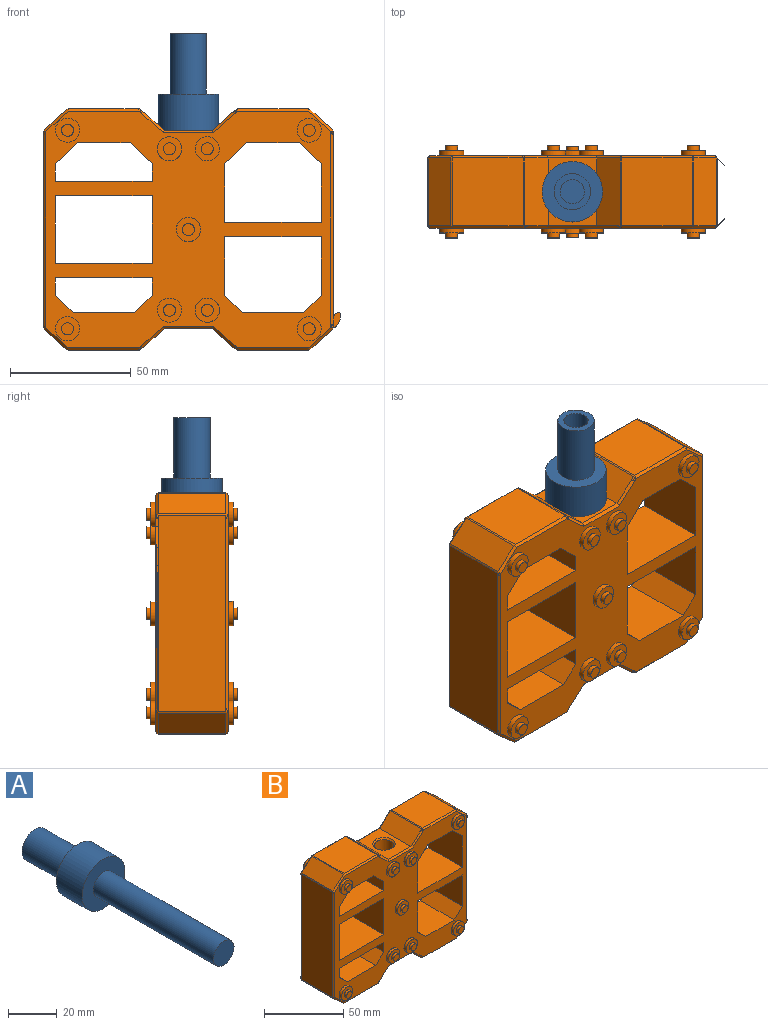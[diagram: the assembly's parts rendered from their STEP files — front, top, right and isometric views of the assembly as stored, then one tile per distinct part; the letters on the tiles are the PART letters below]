
ASSEMBLY  parts=2 mates=1
PART A: 9 faces, bbox 25x110x25 mm
  f0: cylinder r=6mm len=70mm, axis (0,1,0), area 2638.9mm2, adj f1,f4
  f1: plane 12x12mm, normal (0,-1,0), area 113.1mm2, adj f0
  f2: cylinder r=12.5mm len=25mm, axis (0,-1,0), area 1178.1mm2, adj f3,f4
  f3: plane 25x25mm, normal (0,1,0), area 314.2mm2, adj f2,f5
  f4: plane 25x25mm, normal (0,-1,0), area 377.8mm2, adj f0,f2
  f5: cylinder r=7.5mm len=25mm, axis (0,-1,0), area 1178.1mm2, adj f3,f6
  f6: plane 15x15mm, normal (0,1,0), area 98.2mm2, adj f5,f7
  f7: cylinder r=5mm len=25mm, axis (0,1,0), area 785.4mm2, adj f6,f8
  f8: plane 10x10mm, normal (0,1,0), area 78.5mm2, adj f7
PART B: 248 faces, bbox 132.8x46x108 mm
  f0: plane 26.18x0.53mm, normal (-0.18,0,-0.98), area 9mm2, adj f1,f245,f246,f247
  f1: cylinder r=2mm len=0.89mm, axis (-1,0,0), area 0.1mm2, adj f0,f2,f3
  f2: bspline ~2.39x1.21mm, area 0.1mm2, adj f1,f3,f247
  f3: plane 1.1x0.46mm, normal (-0.18,0,-0.98), area 0.3mm2, adj f1,f2,f4,f245,f247
  f4: plane 1x1mm, normal (-0.13,-0.7,-0.7), area 0.3mm2, adj f3,f5,f244
  f5: plane 1.06x1mm, normal (-0.25,-0.71,-0.66), area 0.6mm2, adj f4,f6,f7,f241,f243,f247
  f6: plane 1.28x0.99mm, normal (-0.47,-0.71,-0.53), area 0.2mm2, adj f5,f7,f243
  f7: plane 118x98mm, normal (0,-1,0), area 5531mm2, adj f5,f6,f8,f144,f145,f146,f147,f148
  f8: plane 30x24.21mm, normal (1,0,0), area 726.4mm2, adj f7,f9,f144,f148
  f9: plane 118x98mm, normal (0,1,0), area 5531mm2, adj f8,f10,f14,f18,f22,f26,f30,f34
  f10: cylinder r=5mm len=10mm, axis (0,-1,0), area 62.8mm2, adj f9,f11
  f11: plane 10x10mm, normal (0,1,0), area 58.9mm2, adj f10,f12
  f12: cylinder r=2.5mm len=5mm, axis (0,-1,0), area 31.4mm2, adj f11,f13
  f13: plane 5x5mm, normal (0,1,0), area 19.6mm2, adj f12
  f14: cylinder r=5mm len=10mm, axis (0,-1,0), area 62.8mm2, adj f9,f15
  f15: plane 10x10mm, normal (0,1,0), area 58.9mm2, adj f14,f16
  f16: cylinder r=2.5mm len=5mm, axis (0,-1,0), area 31.4mm2, adj f15,f17
  f17: plane 5x5mm, normal (0,1,0), area 19.6mm2, adj f16
  f18: cylinder r=5mm len=10mm, axis (0,-1,0), area 62.8mm2, adj f9,f19
  f19: plane 10x10mm, normal (0,1,0), area 58.9mm2, adj f18,f20
  f20: cylinder r=2.5mm len=5mm, axis (0,-1,0), area 31.4mm2, adj f19,f21
  f21: plane 5x5mm, normal (0,1,0), area 19.6mm2, adj f20
  f22: cylinder r=5mm len=10mm, axis (0,-1,0), area 62.8mm2, adj f9,f23
  f23: plane 10x10mm, normal (0,1,0), area 58.9mm2, adj f22,f24
  f24: cylinder r=2.5mm len=5mm, axis (0,-1,0), area 31.4mm2, adj f23,f25
  f25: plane 5x5mm, normal (0,1,0), area 19.6mm2, adj f24
  f26: cylinder r=5mm len=10mm, axis (0,-1,0), area 62.8mm2, adj f9,f27
  f27: plane 10x10mm, normal (0,1,0), area 58.9mm2, adj f26,f28
  f28: cylinder r=2.5mm len=5mm, axis (0,-1,0), area 31.4mm2, adj f27,f29
  f29: plane 5x5mm, normal (0,1,0), area 19.6mm2, adj f28
  f30: cylinder r=5mm len=10mm, axis (0,-1,0), area 62.8mm2, adj f9,f31
  f31: plane 10x10mm, normal (0,1,0), area 58.9mm2, adj f30,f32
  f32: cylinder r=2.5mm len=5mm, axis (0,-1,0), area 31.4mm2, adj f31,f33
  f33: plane 5x5mm, normal (0,1,0), area 19.6mm2, adj f32
  f34: cylinder r=5mm len=10mm, axis (0,-1,0), area 62.8mm2, adj f9,f35
  f35: plane 10x10mm, normal (0,1,0), area 58.9mm2, adj f34,f36
  f36: cylinder r=2.5mm len=5mm, axis (0,-1,0), area 31.4mm2, adj f35,f37
  f37: plane 5x5mm, normal (0,1,0), area 19.6mm2, adj f36
  f38: cylinder r=5mm len=10mm, axis (0,-1,0), area 62.8mm2, adj f9,f39
  f39: plane 10x10mm, normal (0,1,0), area 58.9mm2, adj f38,f40
  f40: cylinder r=2.5mm len=5mm, axis (0,-1,0), area 31.4mm2, adj f39,f41
  f41: plane 5x5mm, normal (0,1,0), area 19.6mm2, adj f40
  f42: cylinder r=5mm len=10mm, axis (0,-1,0), area 62.8mm2, adj f9,f43
  f43: plane 10x10mm, normal (0,1,0), area 58.9mm2, adj f42,f44
  f44: cylinder r=2.5mm len=5mm, axis (0,-1,0), area 31.4mm2, adj f43,f45
  f45: plane 5x5mm, normal (0,1,0), area 19.6mm2, adj f44
  f46: plane 10.05x9.1mm, normal (0.47,0.71,0.53), area 17.8mm2, adj f9,f47,f58,f100
  f47: plane 1x1mm, normal (0.67,0.67,0.3), area 0.6mm2, adj f46,f48,f138
  f48: plane 28x0.75mm, normal (0.91,0,0.41), area 22.9mm2, adj f47,f49,f50,f58
  f49: plane 1x1mm, normal (0.67,-0.67,0.3), area 0.6mm2, adj f48,f207,f236
  f50: plane 81.28x28mm, normal (1,0,0), area 2276mm2, adj f48,f51,f138,f236
  f51: plane 28x0.75mm, normal (0.91,0,-0.41), area 22.9mm2, adj f50,f52,f53,f54
  f52: plane 1x1mm, normal (0.67,-0.67,-0.3), area 0.6mm2, adj f51,f235,f236
  f53: plane 1x1mm, normal (0.67,0.67,-0.3), area 0.6mm2, adj f51,f137,f138
  f54: plane 28x9.38mm, normal (0.67,0,-0.75), area 351.8mm2, adj f51,f55,f137,f235
  f55: plane 28x0.67mm, normal (0.36,0,-0.93), area 19.9mm2, adj f54,f56,f57,f245
  f56: plane 1x1mm, normal (0.26,-0.68,-0.68), area 0.5mm2, adj f55,f235,f244
  f57: plane 1x1mm, normal (0.26,0.68,-0.68), area 0.5mm2, adj f55,f136,f137
  f58: plane 28x9.38mm, normal (0.67,0,0.75), area 351.8mm2, adj f46,f48,f59,f207
  f59: plane 28x0.67mm, normal (0.36,0,0.93), area 19.9mm2, adj f58,f60,f61,f100
  f60: plane 1x1mm, normal (0.26,-0.68,0.68), area 0.5mm2, adj f59,f207,f208
  f61: plane 29.24x28mm, normal (0,0,1), area 818.7mm2, adj f59,f62,f101,f208
  f62: plane 28x0.67mm, normal (-0.36,0,0.93), area 19.9mm2, adj f61,f63,f102,f209
  f63: plane 28x9.72mm, normal (-0.67,0,0.75), area 364.3mm2, adj f62,f64,f106,f213
  f64: plane 28x20mm, normal (0,0,1), area 406.1mm2, adj f63,f65,f99,f107,f214
  f65: plane 28x9.72mm, normal (0.67,0,0.75), area 364.3mm2, adj f64,f66,f108,f215
  f66: plane 28x0.67mm, normal (0.36,0,0.93), area 19.9mm2, adj f65,f67,f112,f219
  f67: plane 29.24x28mm, normal (0,0,1), area 818.7mm2, adj f66,f68,f113,f220
  f68: plane 28x0.67mm, normal (-0.36,0,0.93), area 19.9mm2, adj f67,f69,f70,f98
  f69: plane 1x1mm, normal (-0.26,-0.68,0.68), area 0.5mm2, adj f68,f220,f221
  f70: plane 28x9.38mm, normal (-0.67,0,0.75), area 351.8mm2, adj f68,f71,f114,f221
  f71: plane 28x0.75mm, normal (-0.91,0,0.41), area 22.9mm2, adj f70,f72,f73,f97
  f72: plane 1x1mm, normal (-0.67,-0.67,0.3), area 0.6mm2, adj f71,f221,f222
  f73: plane 81.28x28mm, normal (-1,0,0), area 2276mm2, adj f71,f74,f115,f222
  f74: plane 28x0.75mm, normal (-0.91,0,-0.41), area 22.9mm2, adj f73,f75,f76,f96
  f75: plane 1x1mm, normal (-0.67,-0.67,-0.3), area 0.6mm2, adj f74,f222,f227
  f76: plane 28x9.38mm, normal (-0.67,0,-0.75), area 351.8mm2, adj f74,f77,f120,f227
  f77: plane 28x0.67mm, normal (-0.36,0,-0.93), area 19.9mm2, adj f76,f78,f79,f95
  f78: plane 1x1mm, normal (-0.26,-0.68,-0.68), area 0.5mm2, adj f77,f227,f228
  f79: plane 29.05x28mm, normal (0,0,-1), area 813.5mm2, adj f77,f80,f92,f94,f121,f228
  f80: plane 1.1x0.46mm, normal (0.18,0,-0.98), area 0.3mm2, adj f79,f81,f89,f90,f91
  f81: plane 28x0.5mm, normal (0.36,0,-0.93), area 14.8mm2, adj f80,f82,f87,f91,f92,f94,f122,f229
  f82: plane 28x9.72mm, normal (0.67,0,-0.75), area 364.3mm2, adj f81,f83,f126,f233
  f83: plane 28x20mm, normal (0,0,-1), area 406.1mm2, adj f82,f84,f85,f127,f234
  f84: plane 28x9.72mm, normal (-0.67,0,-0.75), area 364.3mm2, adj f83,f128,f241,f247
  f85: cone r=7mm half-angle=45deg, axis (0,0,-1), area 57.8mm2, adj f83,f86
  f86: cylinder r=6mm len=80.18mm, axis (0,0,1), area 3022.8mm2, adj f85,f99
  f87: bspline ~2.39x1.21mm, area 0.1mm2, adj f81,f88,f92,f94
  f88: cylinder r=2mm len=0.89mm, axis (-1,0,0), area 0.1mm2, adj f87,f92,f94
  f89: plane 1x1mm, normal (0.13,0.7,-0.7), area 0.3mm2, adj f80,f121,f122
  f90: cylinder r=2mm len=0.89mm, axis (-1,0,0), area 0.1mm2, adj f80,f91,f94
  f91: bspline ~2.39x1.21mm, area 0.1mm2, adj f80,f81,f90
  f92: plane 1.1x0.46mm, normal (0.18,0,-0.98), area 0.3mm2, adj f79,f81,f87,f88,f93
  f93: plane 1x1mm, normal (0.13,-0.7,-0.7), area 0.3mm2, adj f92,f228,f229
  f94: plane 26.17x0.53mm, normal (0.18,0,-0.98), area 9mm2, adj f79,f81,f87,f88,f90
  f95: plane 1x1mm, normal (-0.26,0.68,-0.68), area 0.5mm2, adj f77,f120,f121
  f96: plane 1x1mm, normal (-0.67,0.67,-0.3), area 0.6mm2, adj f74,f115,f120
  f97: plane 1x1mm, normal (-0.67,0.67,0.3), area 0.6mm2, adj f71,f114,f115
  f98: plane 1x1mm, normal (-0.26,0.68,0.68), area 0.5mm2, adj f68,f113,f114
  f99: cone r=6mm half-angle=45deg, axis (0,0,1), area 57.8mm2, adj f64,f86
  f100: plane 1x1mm, normal (0.26,0.68,0.68), area 0.5mm2, adj f46,f59,f101
  f101: plane 29.24x1mm, normal (0,0.71,0.71), area 41.2mm2, adj f9,f61,f100,f102
  f102: plane 1.13x1mm, normal (-0.25,0.71,0.66), area 0.7mm2, adj f9,f62,f101,f103,f104,f105,f106
  f103: bspline ~1.4x1.27mm, area 1mm2, adj f102,f104,f106
  f104: cylinder r=2mm len=1.34mm, axis (1,0,0), area 0.2mm2, adj f102,f103,f105
  f105: plane 1.28x0.99mm, normal (-0.47,0.71,0.53), area 0.2mm2, adj f9,f102,f104
  f106: plane 10.02x9.69mm, normal (-0.47,0.71,0.53), area 17.2mm2, adj f9,f63,f102,f103,f107
  f107: plane 20.76x1mm, normal (0,0.71,0.71), area 28.8mm2, adj f9,f64,f106,f108
  f108: plane 10.02x9.69mm, normal (0.47,0.71,0.53), area 17.2mm2, adj f9,f65,f107,f109,f112
  f109: bspline ~1.4x1.27mm, area 1mm2, adj f108,f110,f112
  f110: cylinder r=2mm len=1.34mm, axis (1,0,0), area 0.2mm2, adj f109,f111,f112
  f111: plane 1.28x0.99mm, normal (0.47,0.71,0.53), area 0.2mm2, adj f9,f110,f112
  f112: plane 1.13x1mm, normal (0.25,0.71,0.66), area 0.7mm2, adj f9,f66,f108,f109,f110,f111,f113
  f113: plane 29.24x1mm, normal (0,0.71,0.71), area 41.2mm2, adj f9,f67,f98,f112
  f114: plane 10.05x9.1mm, normal (-0.47,0.71,0.53), area 17.8mm2, adj f9,f70,f97,f98
  f115: plane 81.59x1.31mm, normal (-0.71,0.71,0), area 113mm2, adj f9,f73,f96,f97,f116,f117,f118,f119
  f116: bspline ~1.86x1.48mm, area 0.8mm2, adj f115,f117
  f117: cylinder r=2mm len=1.25mm, axis (0.75,0,0.67), area 0mm2, adj f115,f116
  f118: cylinder r=2mm len=1.25mm, axis (-0.75,0,0.67), area 0mm2, adj f115,f119
  f119: bspline ~1.86x1.48mm, area 0.8mm2, adj f115,f118
  f120: plane 10.05x9.1mm, normal (-0.47,0.71,-0.53), area 17.8mm2, adj f9,f76,f95,f96
  f121: plane 29.05x1mm, normal (0,0.71,-0.71), area 41.1mm2, adj f9,f79,f89,f95
  f122: plane 1.06x1mm, normal (0.25,0.71,-0.66), area 0.6mm2, adj f9,f81,f89,f123,f125,f126
  f123: cylinder r=2mm len=1.33mm, axis (-1,0,0), area 0.2mm2, adj f122,f124,f125
  f124: bspline ~1.79x1.67mm, area 1mm2, adj f123,f126
  f125: plane 1.28x0.99mm, normal (0.47,0.71,-0.53), area 0.2mm2, adj f9,f122,f123
  f126: plane 10.22x9.88mm, normal (0.47,0.71,-0.53), area 16.7mm2, adj f9,f82,f122,f124,f127
  f127: plane 20.76x1mm, normal (0,0.71,-0.71), area 28.8mm2, adj f9,f83,f126,f128
  f128: plane 10.22x9.88mm, normal (-0.47,0.71,-0.53), area 17.1mm2, adj f9,f84,f127,f129,f132
  f129: bspline ~1.79x1.67mm, area 1mm2, adj f128,f130
  f130: cylinder r=2mm len=1.33mm, axis (-1,0,0), area 0.2mm2, adj f129,f131,f132
  f131: plane 1.28x0.99mm, normal (-0.47,0.71,-0.53), area 0.2mm2, adj f9,f130,f132
  f132: plane 1.06x1mm, normal (-0.25,0.71,-0.66), area 0.6mm2, adj f9,f128,f130,f131,f133,f247
  f133: plane 1x1mm, normal (-0.13,0.7,-0.7), area 0.3mm2, adj f132,f134,f136
  f134: plane 1.1x0.46mm, normal (-0.18,0,-0.98), area 0.3mm2, adj f133,f135,f245,f246,f247
  f135: bspline ~2.39x1.21mm, area 0.1mm2, adj f134,f246,f247
  f136: plane 29.05x1mm, normal (0,0.71,-0.71), area 41.1mm2, adj f9,f57,f133,f245
  f137: plane 10.05x9.1mm, normal (0.47,0.71,-0.53), area 17.8mm2, adj f9,f53,f54,f57
  f138: plane 89.38x12mm, normal (0.71,0.71,0), area 89.1mm2, adj f9,f47,f50,f53,f139,f140,f141,f142
  f139: cylinder r=2mm len=7.52mm, axis (-0.75,0,-0.67), area 33.7mm2, adj f138
  f140: bspline ~1.86x1.48mm, area 0.8mm2, adj f138,f141
  f141: cylinder r=2mm len=4mm, axis (-0.75,0,-0.67), area 3.4mm2, adj f138,f140
  f142: bspline ~1.86x1.48mm, area 0.8mm2, adj f138,f143
  f143: cylinder r=2mm len=1.25mm, axis (0.75,0,-0.67), area 0mm2, adj f138,f142
  f144: plane 30x7.3mm, normal (0.69,0,0.73), area 302mm2, adj f7,f8,f9,f145
  f145: plane 30x25.39mm, normal (0,0,1), area 761.8mm2, adj f7,f9,f144,f146
  f146: plane 30x7.3mm, normal (-0.69,0,0.73), area 302mm2, adj f7,f9,f145,f147
  f147: plane 30x24.21mm, normal (-1,0,0), area 726.4mm2, adj f7,f9,f146,f148
  f148: plane 40x30mm, normal (0,0,-1), area 1200mm2, adj f7,f8,f9,f147
  f149: plane 30x9.12mm, normal (0.69,0,-0.73), area 376.9mm2, adj f7,f9,f150,f154
  f150: plane 30x24.21mm, normal (1,0,0), area 726.4mm2, adj f7,f9,f149,f151
  f151: plane 40x30mm, normal (0,0,1), area 1200mm2, adj f7,f9,f150,f152
  f152: plane 30x24.21mm, normal (-1,0,0), area 726.4mm2, adj f7,f9,f151,f153
  f153: plane 30x9.12mm, normal (-0.69,0,-0.73), area 376.9mm2, adj f7,f9,f152,f154
  f154: plane 30x21.77mm, normal (0,0,-1), area 653mm2, adj f7,f9,f149,f153
  f155: plane 30x7.21mm, normal (1,0,0), area 216.4mm2, adj f7,f9,f156,f160
  f156: plane 40x30mm, normal (0,0,1), area 1200mm2, adj f7,f9,f155,f157
  f157: plane 30x7.21mm, normal (-1,0,0), area 216.4mm2, adj f7,f9,f156,f158
  f158: plane 30x9.12mm, normal (-0.69,0,-0.73), area 376.9mm2, adj f7,f9,f157,f159
  f159: plane 30x21.77mm, normal (0,0,-1), area 653mm2, adj f7,f9,f158,f160
  f160: plane 30x9.12mm, normal (0.69,0,-0.73), area 376.9mm2, adj f7,f9,f155,f159
  f161: plane 30x28mm, normal (1,0,0), area 840mm2, adj f7,f9,f162,f164
  f162: plane 40x30mm, normal (0,0,1), area 1200mm2, adj f7,f9,f161,f163
  f163: plane 30x28mm, normal (-1,0,0), area 840mm2, adj f7,f9,f162,f164
  f164: plane 40x30mm, normal (0,0,-1), area 1200mm2, adj f7,f9,f161,f163
  f165: plane 30x7.21mm, normal (1,0,0), area 216.4mm2, adj f7,f9,f166,f170
  f166: plane 30x7.3mm, normal (0.69,0,0.73), area 302mm2, adj f7,f9,f165,f167
  f167: plane 30x25.39mm, normal (0,0,1), area 761.8mm2, adj f7,f9,f166,f168
  f168: plane 30x7.3mm, normal (-0.69,0,0.73), area 302mm2, adj f7,f9,f167,f169
  f169: plane 30x7.21mm, normal (-1,0,0), area 216.4mm2, adj f7,f9,f168,f170
  f170: plane 40x30mm, normal (0,0,-1), area 1200mm2, adj f7,f9,f165,f169
  f171: cylinder r=5mm len=10mm, axis (0,1,0), area 62.8mm2, adj f7,f172
  f172: plane 10x10mm, normal (0,-1,0), area 58.9mm2, adj f171,f173
  f173: cylinder r=2.5mm len=5mm, axis (0,1,0), area 31.4mm2, adj f172,f174
  f174: plane 5x5mm, normal (0,-1,0), area 19.6mm2, adj f173
  f175: cylinder r=5mm len=10mm, axis (0,1,0), area 62.8mm2, adj f7,f176
  f176: plane 10x10mm, normal (0,-1,0), area 58.9mm2, adj f175,f177
  f177: cylinder r=2.5mm len=5mm, axis (0,1,0), area 31.4mm2, adj f176,f178
  f178: plane 5x5mm, normal (0,-1,0), area 19.6mm2, adj f177
  f179: cylinder r=5mm len=10mm, axis (0,1,0), area 62.8mm2, adj f7,f180
  f180: plane 10x10mm, normal (0,-1,0), area 58.9mm2, adj f179,f181
  f181: cylinder r=2.5mm len=5mm, axis (0,1,0), area 31.4mm2, adj f180,f182
  f182: plane 5x5mm, normal (0,-1,0), area 19.6mm2, adj f181
  f183: cylinder r=5mm len=10mm, axis (0,1,0), area 62.8mm2, adj f7,f184
  f184: plane 10x10mm, normal (0,-1,0), area 58.9mm2, adj f183,f185
  f185: cylinder r=2.5mm len=5mm, axis (0,1,0), area 31.4mm2, adj f184,f186
  f186: plane 5x5mm, normal (0,-1,0), area 19.6mm2, adj f185
  f187: cylinder r=5mm len=10mm, axis (0,1,0), area 62.8mm2, adj f7,f188
  f188: plane 10x10mm, normal (0,-1,0), area 58.9mm2, adj f187,f189
  f189: cylinder r=2.5mm len=5mm, axis (0,1,0), area 31.4mm2, adj f188,f190
  f190: plane 5x5mm, normal (0,-1,0), area 19.6mm2, adj f189
  f191: cylinder r=5mm len=10mm, axis (0,1,0), area 62.8mm2, adj f7,f192
  f192: plane 10x10mm, normal (0,-1,0), area 58.9mm2, adj f191,f193
  f193: cylinder r=2.5mm len=5mm, axis (0,1,0), area 31.4mm2, adj f192,f194
  f194: plane 5x5mm, normal (0,-1,0), area 19.6mm2, adj f193
  f195: cylinder r=5mm len=10mm, axis (0,1,0), area 62.8mm2, adj f7,f196
  f196: plane 10x10mm, normal (0,-1,0), area 58.9mm2, adj f195,f197
  f197: cylinder r=2.5mm len=5mm, axis (0,1,0), area 31.4mm2, adj f196,f198
  f198: plane 5x5mm, normal (0,-1,0), area 19.6mm2, adj f197
  f199: cylinder r=5mm len=10mm, axis (0,1,0), area 62.8mm2, adj f7,f200
  f200: plane 10x10mm, normal (0,-1,0), area 58.9mm2, adj f199,f201
  f201: cylinder r=2.5mm len=5mm, axis (0,1,0), area 31.4mm2, adj f200,f202
  f202: plane 5x5mm, normal (0,-1,0), area 19.6mm2, adj f201
  f203: cylinder r=5mm len=10mm, axis (0,1,0), area 62.8mm2, adj f7,f204
  f204: plane 10x10mm, normal (0,-1,0), area 58.9mm2, adj f203,f205
  f205: cylinder r=2.5mm len=5mm, axis (0,1,0), area 31.4mm2, adj f204,f206
  f206: plane 5x5mm, normal (0,-1,0), area 19.6mm2, adj f205
  f207: plane 10.05x9.1mm, normal (0.47,-0.71,0.53), area 17.8mm2, adj f7,f49,f58,f60
  f208: plane 29.24x1mm, normal (0,-0.71,0.71), area 41.2mm2, adj f7,f60,f61,f209
  f209: plane 1.13x1mm, normal (-0.25,-0.71,0.66), area 0.7mm2, adj f7,f62,f208,f210,f211,f212,f213
  f210: bspline ~1.79x1.67mm, area 1mm2, adj f209,f211,f213
  f211: cylinder r=2mm len=1.34mm, axis (1,0,0), area 0.2mm2, adj f209,f210,f212
  f212: plane 1.28x0.99mm, normal (-0.47,-0.71,0.53), area 0.2mm2, adj f7,f209,f211
  f213: plane 10.02x9.69mm, normal (-0.47,-0.71,0.53), area 17.2mm2, adj f7,f63,f209,f210,f214
  f214: plane 20.76x1mm, normal (0,-0.71,0.71), area 28.8mm2, adj f7,f64,f213,f215
  f215: plane 10.02x9.69mm, normal (0.47,-0.71,0.53), area 17.2mm2, adj f7,f65,f214,f216,f219
  f216: bspline ~1.79x1.67mm, area 1mm2, adj f215,f217,f219
  f217: cylinder r=2mm len=1.34mm, axis (1,0,0), area 0.2mm2, adj f216,f218,f219
  f218: plane 1.28x0.99mm, normal (0.47,-0.71,0.53), area 0.2mm2, adj f7,f217,f219
  f219: plane 1.13x1mm, normal (0.25,-0.71,0.66), area 0.7mm2, adj f7,f66,f215,f216,f217,f218,f220
  f220: plane 29.24x1mm, normal (0,-0.71,0.71), area 41.2mm2, adj f7,f67,f69,f219
  f221: plane 10.05x9.1mm, normal (-0.47,-0.71,0.53), area 17.8mm2, adj f7,f69,f70,f72
  f222: plane 81.41x1.12mm, normal (-0.71,-0.71,0), area 112.9mm2, adj f7,f72,f73,f75,f223,f224,f225,f226
  f223: cylinder r=2mm len=1.25mm, axis (-0.75,0,0.67), area 0.1mm2, adj f222,f224
  f224: bspline ~1.86x1.48mm, area 0.8mm2, adj f222,f223
  f225: bspline ~1.86x1.48mm, area 0.8mm2, adj f222,f226
  f226: cylinder r=2mm len=1.25mm, axis (0.75,0,0.67), area 0.1mm2, adj f222,f225
  f227: plane 10.05x9.1mm, normal (-0.47,-0.71,-0.53), area 17.8mm2, adj f7,f75,f76,f78
  f228: plane 29.05x1mm, normal (0,-0.71,-0.71), area 41.1mm2, adj f7,f78,f79,f93
  f229: plane 1.06x1mm, normal (0.25,-0.71,-0.66), area 0.6mm2, adj f7,f81,f93,f230,f232,f233
  f230: cylinder r=2mm len=1.34mm, axis (-1,0,0), area 0.2mm2, adj f229,f231,f232
  f231: bspline ~1.79x1.67mm, area 1mm2, adj f230,f233
  f232: plane 1.28x0.99mm, normal (0.47,-0.71,-0.53), area 0.2mm2, adj f7,f229,f230
  f233: plane 10.23x9.88mm, normal (0.47,-0.71,-0.53), area 17.1mm2, adj f7,f82,f229,f231,f234
  f234: plane 20.76x1mm, normal (0,-0.71,-0.71), area 28.8mm2, adj f7,f83,f233,f241
  f235: plane 10.05x9.1mm, normal (0.47,-0.71,-0.53), area 17.8mm2, adj f7,f52,f54,f56
  f236: plane 81.41x1.12mm, normal (0.71,-0.71,0), area 113mm2, adj f7,f49,f50,f52,f237,f238,f239,f240
  f237: cylinder r=2mm len=1.25mm, axis (0.75,0,-0.67), area 0.1mm2, adj f236,f238
  f238: bspline ~1.86x1.48mm, area 0.8mm2, adj f236,f237
  f239: bspline ~1.86x1.48mm, area 0.8mm2, adj f236,f240
  f240: cylinder r=2mm len=1.25mm, axis (-0.75,0,-0.67), area 0.1mm2, adj f236,f239
  f241: plane 10.22x9.88mm, normal (-0.47,-0.71,-0.53), area 16.7mm2, adj f5,f7,f84,f234,f242
  f242: bspline ~1.79x1.67mm, area 1mm2, adj f241,f243
  f243: cylinder r=2mm len=1.33mm, axis (-1,0,0), area 0.2mm2, adj f5,f6,f242
  f244: plane 29.05x1mm, normal (0,-0.71,-0.71), area 41.1mm2, adj f4,f7,f56,f245
  f245: plane 29.05x28mm, normal (0,0,-1), area 813.5mm2, adj f0,f3,f55,f134,f136,f244
  f246: cylinder r=2mm len=0.89mm, axis (-1,0,0), area 0.1mm2, adj f0,f134,f135
  f247: plane 28x0.5mm, normal (-0.36,0,-0.93), area 14.8mm2, adj f0,f2,f3,f5,f84,f132,f134,f135
PLACE A rot(axis=(1,0,0),90deg) t=(-9.72,-10.35,34)mm
PLACE B t=(-44.72,4.65,-7.09)mm
MATE revolute A.f0 <-> B.f85  axis (0,0,1) through (-9.72,-10.35,34)mm
